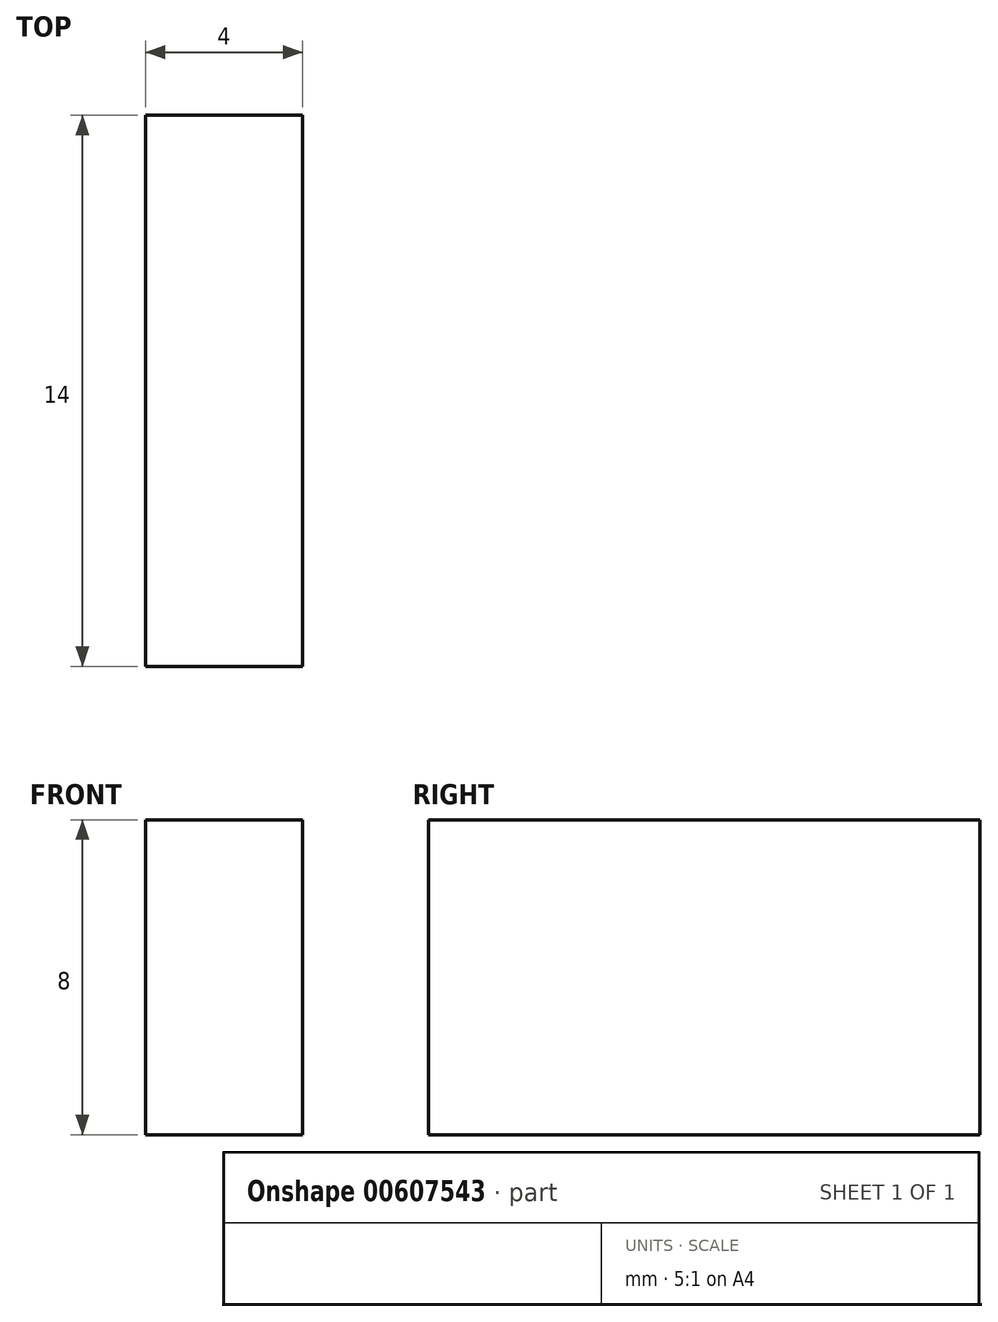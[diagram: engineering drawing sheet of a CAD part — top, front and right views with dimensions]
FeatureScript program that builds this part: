
annotation { "Feature Type Name" : "Feature", "Feature Type Description" : "" }
export const myFeature = defineFeature(function(context is Context, id is Id, definition is map)
    precondition{}
    {
        {
            var Q0;
            Q0=qCreatedBy(makeId("Top.planeOp"),FACE);
            var sketch = newSketch(context, id + "F0", { "sketchPlane" : qUnion([Q0])});
            skLineSegment(sketch, "E0.bottom", {"start": v(-4, 7) * mm, "end": v(0, 7) * mm});
            skLineSegment(sketch, "E0.top", {"start": v(-4, -7) * mm, "end": v(0, -7) * mm});
            skLineSegment(sketch, "E0.left", {"start": v(-4, 7) * mm, "end": v(-4, -7) * mm});
            skLineSegment(sketch, "E0.right", {"start": v(0, 7) * mm, "end": v(0, -7) * mm});
            skPoint(sketch, "E1", {"position": v(0, 0) * mm});
            skSolve(sketch);
        }
        {
            var Q0;
            Q0 = qSketchRegion(id + "F0", true);
            extrude(context, id + "F1", {"entities" : qUnion([Q0]), "depth" : 8 * mm, "offsetDistance" : 25 * mm});
        }
    });
